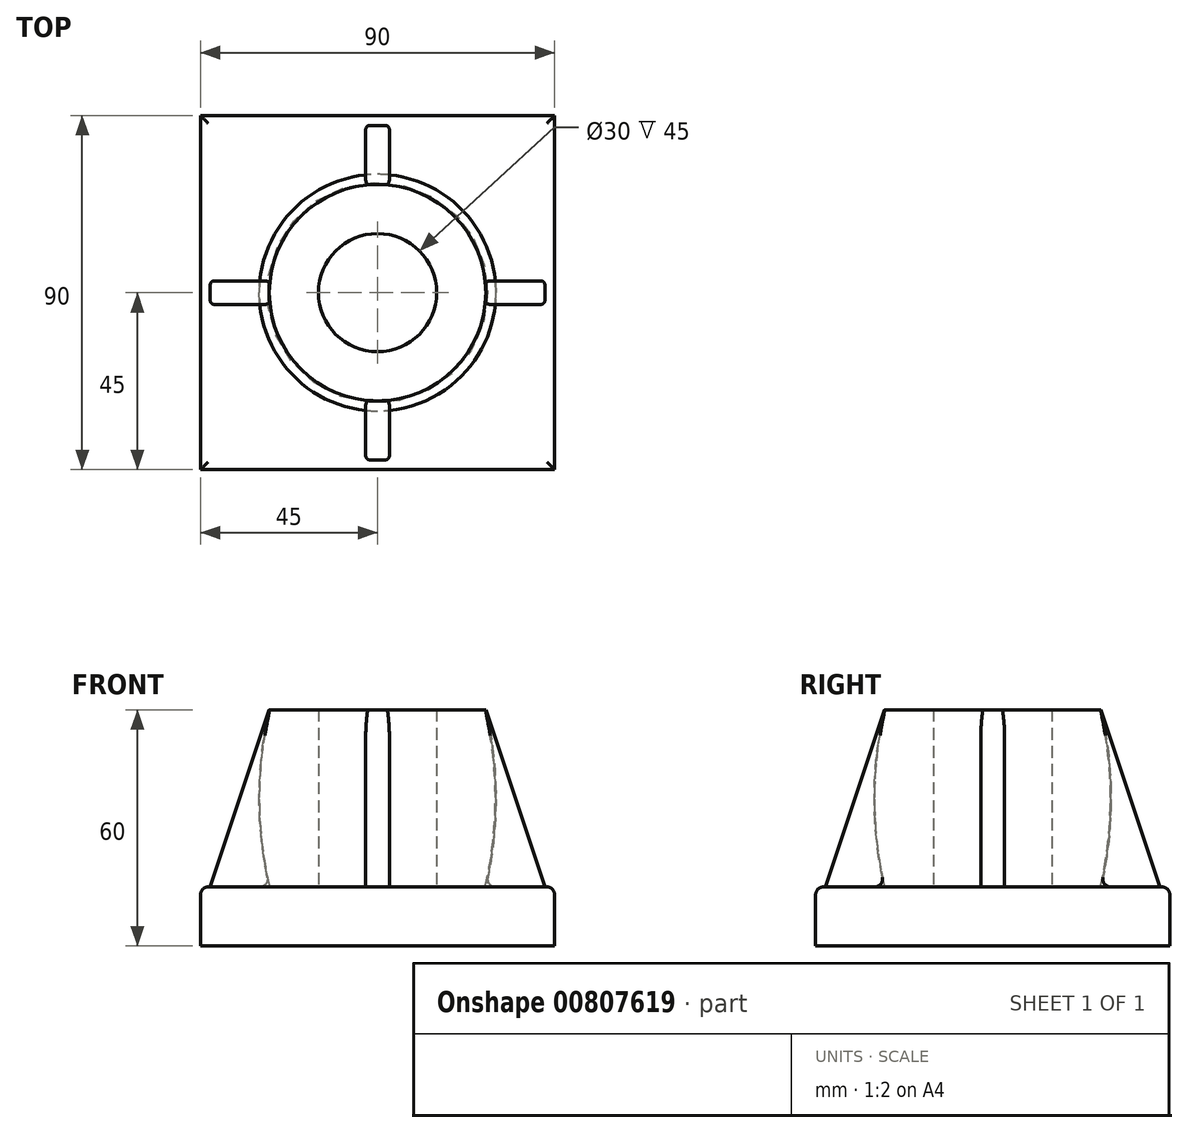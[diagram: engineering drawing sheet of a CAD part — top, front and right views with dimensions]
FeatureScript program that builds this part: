
annotation { "Feature Type Name" : "Feature", "Feature Type Description" : "" }
export const myFeature = defineFeature(function(context is Context, id is Id, definition is map)
    precondition{}
    {
        {
            var Q0;
            Q0=qCreatedBy(makeId("Top.planeOp"),FACE);
            var sketch = newSketch(context, id + "F0", { "sketchPlane" : qUnion([Q0])});
            skLineSegment(sketch, "E0.bottom", {"start": v(45, 45) * mm, "end": v(-45, 45) * mm});
            skLineSegment(sketch, "E0.top", {"start": v(45, -45) * mm, "end": v(-45, -45) * mm});
            skLineSegment(sketch, "E0.left", {"start": v(45, 45) * mm, "end": v(45, -45) * mm});
            skLineSegment(sketch, "E0.right", {"start": v(-45, 45) * mm, "end": v(-45, -45) * mm});
            skPoint(sketch, "E0.middle", {"position": v(0, 0) * mm});
            skSolve(sketch);
        }
        {
            var Q0;
            Q0 = qSketchRegion(id + "F0", true);
            extrude(context, id + "F1", {"entities" : qUnion([Q0]), "depth" : 15 * mm, "offsetDistance" : 25 * mm});
        }
        {
            var Q0;
            Q0=qCreatedBy(makeId("Front.planeOp"),FACE);
            var sketch = newSketch(context, id + "F2", { "sketchPlane" : qUnion([Q0])});
            skLineSegment(sketch, "E1.0", {"start": v(45, 15) * mm, "end": v(-45, 15) * mm});
            skLineSegment(sketch, "E2", {"start": v(-15, 15) * mm, "end": v(-15, 60) * mm});
            skLineSegment(sketch, "E3", {"start": v(-15, 60) * mm, "end": v(-27.5, 60) * mm});
            skArc(sketch, "E4", {"start": v(-27.5, 60) * mm, "mid": v(-30.06, 37.5) * mm, "end": v(-27.5, 15) * mm});
            skLineSegment(sketch, "E5", {"start": v(0, 0) * mm, "end": v(0, 55) * mm, "construction": true});
            skSolve(sketch);
        }
        {
            var Q0;
            {var subQ0=sQuery(id+"F2.wireOp",EDGE,"E2");Q0=makeQuery(id+"F2.imprint","IMPRINT",FACE,{"disambiguationData":[TD([[makeQuery(id+"F2.imprint","IMPRINT",EDGE,{"derivedFrom":subQ0}),1.0]])]});}
            var Q1;
            Q1=sQuery(id+"F2.wireOp",EDGE,"E5");
            revolve(context, id + "F3", {"operationType" : NewBodyOperationType.ADD, "surfaceOperationType" : NewSurfaceOperationType.NEW, "entities" : qUnion([Q0]), "axis" : qUnion([Q1]), "revolveType" : RevolveType.FULL});
        }
        {
            var Q0;
            Q0=qCreatedBy(makeId("Front.planeOp"),FACE);
            var sketch = newSketch(context, id + "F4", { "sketchPlane" : qUnion([Q0])});
            skLineSegment(sketch, "E6.0.0", {"start": v(-45, 0) * mm, "end": v(45, 0) * mm});
            skLineSegment(sketch, "E6.0.1", {"start": v(45, 0) * mm, "end": v(45, 15) * mm});
            skLineSegment(sketch, "E6.0.2", {"start": v(45, 15) * mm, "end": v(-42.5, 15) * mm});
            skLineSegment(sketch, "E6.0.3", {"start": v(-45, 15) * mm, "end": v(-45, 0) * mm});
            skPoint(sketch, "E7.0", {"position": v(-27.5, 60) * mm});
            skPoint(sketch, "E8.0", {"position": v(-45, 15) * mm});
            skLineSegment(sketch, "E9", {"start": v(-42.5, 15) * mm, "end": v(-27.5, 60) * mm});
            skLineSegment(sketch, "E10", {"start": v(-27.5, 60) * mm, "end": v(-22.5, 60) * mm});
            skLineSegment(sketch, "E11", {"start": v(-22.5, 60) * mm, "end": v(-22.5, 15) * mm});
            skLineSegment(sketch, "E12", {"start": v(-22.5, 15) * mm, "end": v(-42.5, 15) * mm});
            skSolve(sketch);
        }
        {
            var Q0;
            Q0=makeQuery(id+"F4.imprint","IMPRINT",FACE,{"disambiguationData":[TD([[makeQuery(id+"F4.imprint","IMPRINT",EDGE,{"derivedFrom":sQuery(id+"F4.wireOp",EDGE,"E9")}),-1.0]])]});
            extrude(context, id + "F5", {"entities" : qUnion([Q0]), "depth" : 6 * mm, "offsetDistance" : 25 * mm, "symmetric" : true});
        }
        {
            var Q0;
            Q0=makeQuery(id+"F1.opExtrude","SWEPT_BODY",BODY,{"disambiguationData":[OSD([sQuery(id+"F0.wireOp",EDGE,"E0.bottom"),sQuery(id+"F0.wireOp",EDGE,"E0.top"),sQuery(id+"F0.wireOp",EDGE,"E0.left"),sQuery(id+"F0.wireOp",EDGE,"E0.right")])]});
            var Q1;
            Q1=makeQuery(id+"F5.opExtrude","SWEPT_BODY",BODY,{"disambiguationData":[OSD([sQuery(id+"F4.wireOp",EDGE,"E9"),sQuery(id+"F4.wireOp",EDGE,"E10"),sQuery(id+"F4.wireOp",EDGE,"E11"),sQuery(id+"F4.wireOp",EDGE,"E12")])]});
            booleanBodies(context, id + "F6", {"operationType" : BooleanOperationType.SUBTRACTION, "tools" : qUnion([Q0]), "targets" : qUnion([Q1]), "keepTools" : true});
        }
        {
            var Q0;
            Q0=makeQuery(id+"F5.opExtrude","SWEPT_BODY",BODY,{"disambiguationData":[OSD([sQuery(id+"F4.wireOp",EDGE,"E9"),sQuery(id+"F4.wireOp",EDGE,"E10"),sQuery(id+"F4.wireOp",EDGE,"E11"),sQuery(id+"F4.wireOp",EDGE,"E12")])]});
            var Q1;
            Q1=sQuery(id+"F2.wireOp",EDGE,"E5");
            circularPattern(context, id + "F7", {"entities" : qUnion([Q0]), "axis" : qUnion([Q1]), "angle" : 360 * degree, "instanceCount" : 4, "equalSpace" : true, "computeTransformsWithoutBuiltin" : true});
        }
        {
            var Q0;
            {var subQ0=sQuery(id+"F0.wireOp",EDGE,"E0.left");var subQ1=sQuery(id+"F0.wireOp",EDGE,"E0.top");var subQ2=sQuery(id+"F0.wireOp",EDGE,"E0.right");var subQ3=sQuery(id+"F0.wireOp",EDGE,"E0.bottom");Q0=makeQuery(id+"F3.boolean.opBoolean","SPLIT",FACE,{"disambiguationData":[TD([makeQuery(id+"F1.opExtrude","SWEPT_FACE",FACE,{"disambiguationData":[OSD([subQ3])]})])],"derivedFrom":makeQuery(id+"F1.opExtrude","CAP_FACE",FACE,{"disambiguationData":[OSD([subQ3,subQ1,subQ0,subQ2])],"isStart":false})});}
            fillet(context, id + "F8", {"entities" : qUnion([Q0]), "radius" : 2 * mm, "tangentPropagation" : true, "allowEdgeOverflow" : false});
        }
        {
            var Q0;
            Q0=makeQuery(id+"F5.opExtrude","CAP_EDGE",EDGE,{"disambiguationData":[OSD([sQuery(id+"F4.wireOp",EDGE,"E9")])],"isStart":true});
            var Q1;
            Q1=makeQuery(id+"F5.opExtrude","CAP_EDGE",EDGE,{"disambiguationData":[OSD([sQuery(id+"F4.wireOp",EDGE,"E9")])],"isStart":false});
            fillet(context, id + "F9", {"entities" : qUnion([Q0, Q1]), "radius" : 1 * mm, "tangentPropagation" : true, "allowEdgeOverflow" : false});
        }
        {
            var Q0;
            Q0=makeQuery(id+"F7.opPattern","COPY",EDGE,{"derivedFrom":makeQuery(id+"F5.opExtrude","CAP_EDGE",EDGE,{"disambiguationData":[OSD([sQuery(id+"F4.wireOp",EDGE,"E9")])],"isStart":false}),"instanceName":"3"});
            var Q1;
            Q1=makeQuery(id+"F7.opPattern","COPY",EDGE,{"derivedFrom":makeQuery(id+"F5.opExtrude","CAP_EDGE",EDGE,{"disambiguationData":[OSD([sQuery(id+"F4.wireOp",EDGE,"E9")])],"isStart":true}),"instanceName":"3"});
            var Q2;
            Q2=makeQuery(id+"F7.opPattern","COPY",EDGE,{"derivedFrom":makeQuery(id+"F5.opExtrude","CAP_EDGE",EDGE,{"disambiguationData":[OSD([sQuery(id+"F4.wireOp",EDGE,"E9")])],"isStart":true}),"instanceName":"2"});
            var Q3;
            Q3=makeQuery(id+"F7.opPattern","COPY",EDGE,{"derivedFrom":makeQuery(id+"F5.opExtrude","CAP_EDGE",EDGE,{"disambiguationData":[OSD([sQuery(id+"F4.wireOp",EDGE,"E9")])],"isStart":false}),"instanceName":"2"});
            var Q4;
            Q4=makeQuery(id+"F7.opPattern","COPY",EDGE,{"derivedFrom":makeQuery(id+"F5.opExtrude","CAP_EDGE",EDGE,{"disambiguationData":[OSD([sQuery(id+"F4.wireOp",EDGE,"E9")])],"isStart":false}),"instanceName":"1"});
            var Q5;
            Q5=makeQuery(id+"F7.opPattern","COPY",EDGE,{"derivedFrom":makeQuery(id+"F5.opExtrude","CAP_EDGE",EDGE,{"disambiguationData":[OSD([sQuery(id+"F4.wireOp",EDGE,"E9")])],"isStart":true}),"instanceName":"1"});
            fillet(context, id + "F10", {"entities" : qUnion([Q0, Q1, Q2, Q3, Q4, Q5]), "radius" : 1 * mm, "tangentPropagation" : true, "allowEdgeOverflow" : false});
        }
    });
